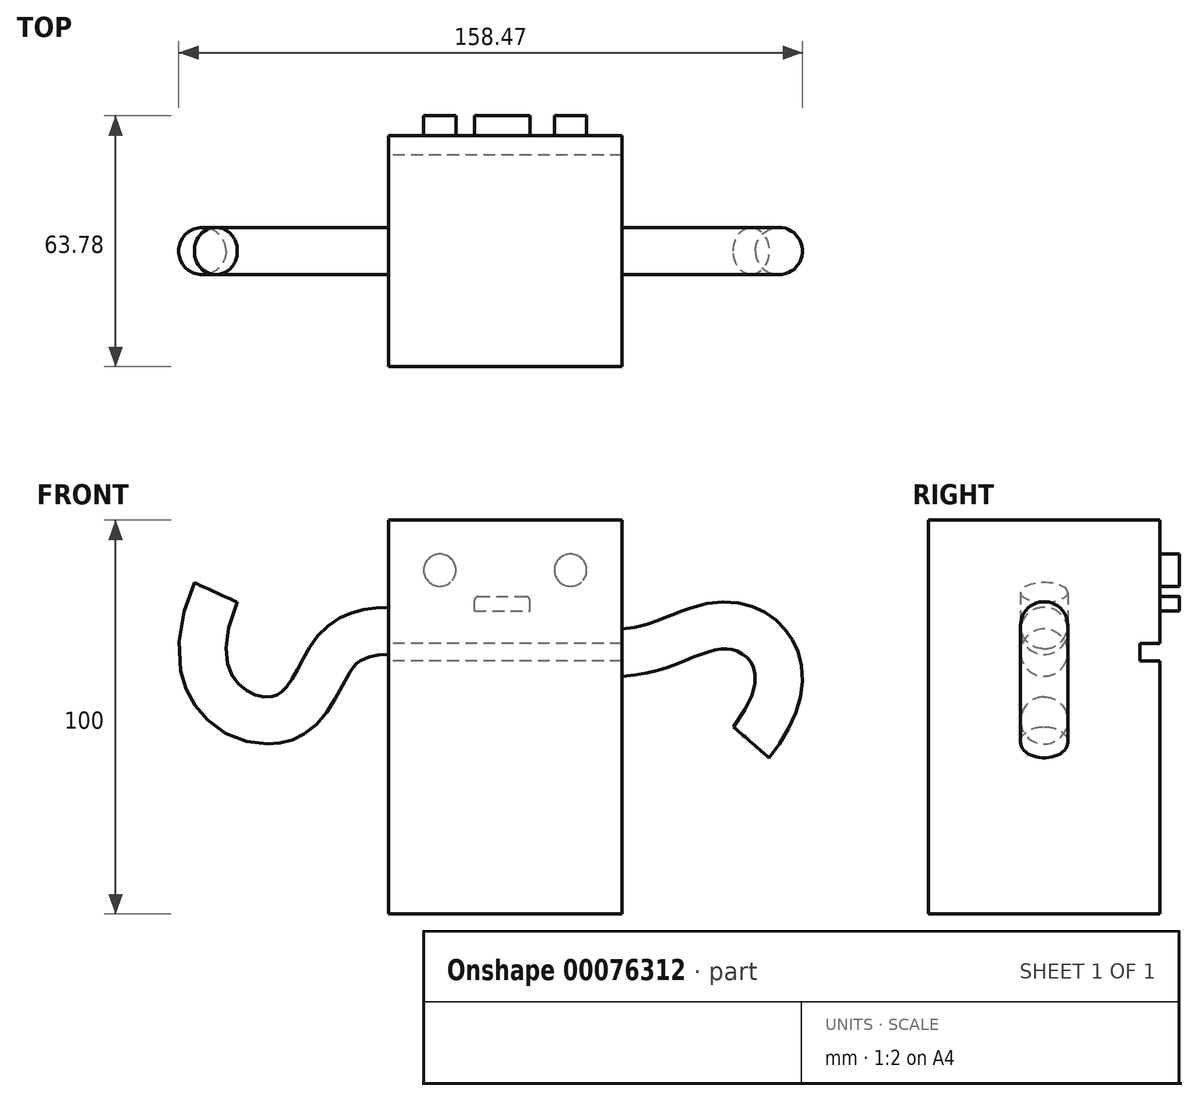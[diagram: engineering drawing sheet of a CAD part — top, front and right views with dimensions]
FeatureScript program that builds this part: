
annotation { "Feature Type Name" : "Feature", "Feature Type Description" : "" }
export const myFeature = defineFeature(function(context is Context, id is Id, definition is map)
    precondition{}
    {
        {
            var Q0;
            Q0=qCreatedBy(makeId("Top.planeOp"),FACE);
            var sketch = newSketch(context, id + "F0", { "sketchPlane" : qUnion([Q0])});
            skLineSegment(sketch, "E0.bottom", {"start": v(29.68, 29.39) * mm, "end": v(-29.68, 29.39) * mm});
            skLineSegment(sketch, "E0.top", {"start": v(29.68, -29.39) * mm, "end": v(-29.68, -29.39) * mm});
            skLineSegment(sketch, "E0.left", {"start": v(29.68, 29.39) * mm, "end": v(29.68, -29.39) * mm});
            skLineSegment(sketch, "E0.right", {"start": v(-29.68, 29.39) * mm, "end": v(-29.68, -29.39) * mm});
            skPoint(sketch, "E0.middle", {"position": v(0, 0) * mm});
            skSolve(sketch);
        }
        {
            var Q0;
            Q0 = qSketchRegion(id + "F0", true);
            extrude(context, id + "F1", {"entities" : qUnion([Q0]), "depth" : 100 * mm});
        }
        {
            var Q0;
            Q0=makeQuery(id+"F1.opExtrude","SWEPT_FACE",FACE,{"disambiguationData":[OSD([sQuery(id+"F0.wireOp",EDGE,"E0.left")])]});
            var sketch = newSketch(context, id + "F2", { "sketchPlane" : qUnion([Q0])});
            skCircle(sketch, "E1", {"center": v(0, 66.37) * mm, "radius": 6 * mm});
            skSolve(sketch);
        }
        {
            var Q0;
            Q0=qCreatedBy(makeId("Front.planeOp"),FACE);
            var sketch = newSketch(context, id + "F3", { "sketchPlane" : qUnion([Q0])});
            skFitSpline(sketch, "E2", {"points": [v(29.7, 66.36) * mm, v(46.1, 70.97) * mm, v(61.14, 72.3) * mm, v(62.47, 43.57) * mm], "startDerivative": vector(66.55, 3.29) * mm, "endDerivative": vector(-95, -120) * mm});
            skSolve(sketch);
        }
        {
            var Q0;
            Q0=makeQuery(id+"F2.imprint","IMPRINT",FACE,{"disambiguationData":[TD([[makeQuery(id+"F2.imprint","IMPRINT",EDGE,{"derivedFrom":sQuery(id+"F2.wireOp",EDGE,"E1")}),1.0]])]});
            var Q1;
            Q1=sQuery(id+"F3.wireOp",EDGE,"E2");
            sweep(context, id + "F4", {"operationType" : NewBodyOperationType.ADD, "profiles" : qUnion([Q0]), "path" : qUnion([Q1])});
        }
        {
            var Q0;
            Q0=makeQuery(id+"F1.opExtrude","SWEPT_FACE",FACE,{"disambiguationData":[OSD([sQuery(id+"F0.wireOp",EDGE,"E0.right")])]});
            var sketch = newSketch(context, id + "F5", { "sketchPlane" : qUnion([Q0])});
            skCircle(sketch, "E3", {"center": v(0, 71.88) * mm, "radius": 6 * mm});
            skSolve(sketch);
        }
        {
            var Q0;
            Q0=qCreatedBy(makeId("Front.planeOp"),FACE);
            var sketch = newSketch(context, id + "F6", { "sketchPlane" : qUnion([Q0])});
            skFitSpline(sketch, "E4", {"points": [v(-29.68, 71.86) * mm, v(-43.09, 66.6) * mm, v(-56.82, 49.58) * mm, v(-73.53, 81.66) * mm], "startDerivative": vector(-62.42, -1.25) * mm, "endDerivative": vector(79.67, 183.47) * mm});
            skSolve(sketch);
        }
        {
            var Q0;
            Q0=makeQuery(id+"F5.imprint","IMPRINT",FACE,{"disambiguationData":[TD([[makeQuery(id+"F5.imprint","IMPRINT",EDGE,{"derivedFrom":sQuery(id+"F5.wireOp",EDGE,"E3")}),1.0]])]});
            var Q1;
            Q1=sQuery(id+"F6.wireOp",EDGE,"E4");
            sweep(context, id + "F7", {"operationType" : NewBodyOperationType.ADD, "profiles" : qUnion([Q0]), "path" : qUnion([Q1])});
        }
        {
            var Q0;
            Q0=makeQuery(id+"F1.opExtrude","SWEPT_FACE",FACE,{"disambiguationData":[OSD([sQuery(id+"F0.wireOp",EDGE,"E0.bottom")])]});
            var sketch = newSketch(context, id + "F8", { "sketchPlane" : qUnion([Q0])});
            skLineSegment(sketch, "E5.bottom", {"start": v(-31.32, 64.28) * mm, "end": v(32.07, 64.28) * mm});
            skLineSegment(sketch, "E5.top", {"start": v(-31.32, 68.7) * mm, "end": v(32.07, 68.7) * mm});
            skLineSegment(sketch, "E5.left", {"start": v(-31.32, 64.28) * mm, "end": v(-31.32, 68.7) * mm});
            skLineSegment(sketch, "E5.right", {"start": v(32.07, 64.28) * mm, "end": v(32.07, 68.7) * mm});
            skSolve(sketch);
        }
        {
            var Q0;
            Q0 = qSketchRegion(id + "F8", true);
            extrude(context, id + "F9", {"entities" : qUnion([Q0]), "operationType" : NewBodyOperationType.REMOVE, "oppositeDirection" : true, "depth" : 5 * mm});
        }
        {
            var Q0;
            {var subQ2=sQuery(id+"F0.wireOp",EDGE,"E0.bottom");Q0=makeQuery(id+"F9.boolean.opBoolean","SPLIT",FACE,{"disambiguationData":[TD([makeQuery(id+"F9.opExtrude","SWEPT_FACE",FACE,{"disambiguationData":[OSD([sQuery(id+"F8.wireOp",EDGE,"E5.top")])]})])],"derivedFrom":makeQuery(id+"F1.opExtrude","SWEPT_FACE",FACE,{"disambiguationData":[OSD([subQ2])]})});}
            var sketch = newSketch(context, id + "F10", { "sketchPlane" : qUnion([Q0])});
            skCircle(sketch, "E6", {"center": v(-16.6, 87.31) * mm, "radius": 4.1 * mm});
            skCircle(sketch, "E7.MirrorC", {"center": v(16.6, 87.31) * mm, "radius": 4.1 * mm});
            skLineSegment(sketch, "E8.bottom", {"start": v(7.82, 76.97) * mm, "end": v(-6.29, 76.97) * mm});
            skLineSegment(sketch, "E8.top", {"start": v(6.82, 80.58) * mm, "end": v(-5.29, 80.58) * mm});
            skLineSegment(sketch, "E8.left", {"start": v(7.82, 76.97) * mm, "end": v(7.82, 79.58) * mm});
            skLineSegment(sketch, "E8.right", {"start": v(-6.29, 76.97) * mm, "end": v(-6.29, 79.58) * mm});
            skPoint(sketch, "E9.visualSharp", {"position": v(7.82, 80.58) * mm});
            skArc(sketch, "E9.filletArc", {"start": v(7.82, 79.58) * mm, "mid": v(7.53, 80.29) * mm, "end": v(6.82, 80.58) * mm});
            skPoint(sketch, "E10.visualSharp", {"position": v(-6.29, 80.58) * mm});
            skArc(sketch, "E10.filletArc", {"start": v(-5.29, 80.58) * mm, "mid": v(-6, 80.29) * mm, "end": v(-6.29, 79.58) * mm});
            skSolve(sketch);
        }
        {
            var Q0;
            Q0 = qSketchRegion(id + "F10", true);
            extrude(context, id + "F11", {"entities" : qUnion([Q0]), "operationType" : NewBodyOperationType.ADD, "depth" : 5 * mm});
        }
    });
